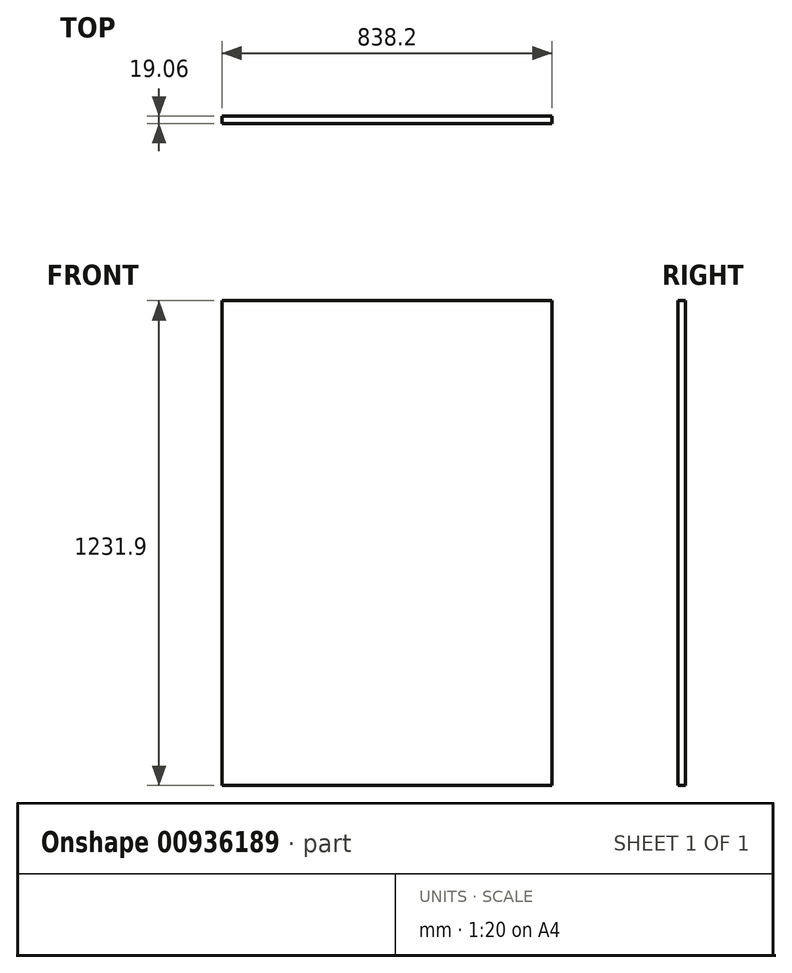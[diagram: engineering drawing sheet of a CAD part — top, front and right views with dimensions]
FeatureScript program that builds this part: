
annotation { "Feature Type Name" : "Feature", "Feature Type Description" : "" }
export const myFeature = defineFeature(function(context is Context, id is Id, definition is map)
    precondition{}
    {
        {
            var Q0;
            Q0=qCreatedBy(makeId("Front.planeOp"),FACE);
            var sketch = newSketch(context, id + "F0", { "sketchPlane" : qUnion([Q0])});
            skPoint(sketch, "E0.middle", {"position": v(0, 0) * mm});
            skLineSegment(sketch, "E1.bottom", {"start": v(419.1, -615.95) * mm, "end": v(-419.1, -615.95) * mm});
            skLineSegment(sketch, "E1.top", {"start": v(419.1, 615.95) * mm, "end": v(-419.1, 615.95) * mm});
            skLineSegment(sketch, "E1.left", {"start": v(419.1, -615.95) * mm, "end": v(419.1, 615.95) * mm});
            skLineSegment(sketch, "E1.right", {"start": v(-419.1, -615.95) * mm, "end": v(-419.1, 615.95) * mm});
            skSolve(sketch);
        }
        {
            var Q0;
            Q0=makeQuery(id+"F0.imprint","IMPRINT",FACE,{"disambiguationData":[TD([[makeQuery(id+"F0.imprint","IMPRINT",EDGE,{"derivedFrom":sQuery(id+"F0.wireOp",EDGE,"E1.bottom")}),-1.0]])]});
            extrude(context, id + "F1", {"entities" : qUnion([Q0]), "endBound" : BoundingType.SYMMETRIC, "depth" : 19.05 * mm, "offsetDistance" : 25.4 * mm});
        }
    });
